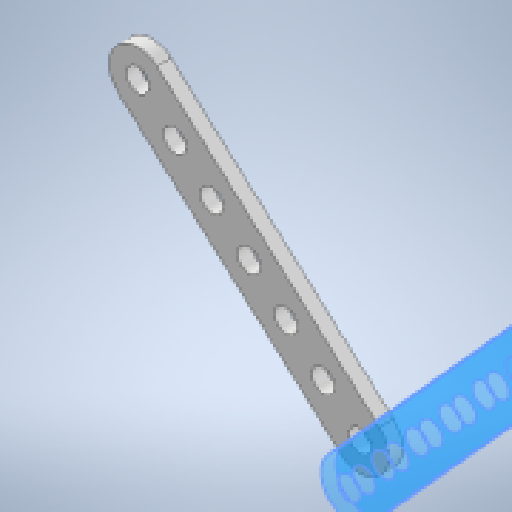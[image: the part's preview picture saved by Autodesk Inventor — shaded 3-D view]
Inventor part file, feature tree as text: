
AUTODESK INVENTOR PART (.ipt)
format: ipt  version: 2024.1 (Build 281209000, 209)  size: 167,936 bytes
history: native  units: mm
features: other x3, extrude x1, fillet x1, sketch x1, reference x1
ambient origin geometry x8: Origin, YZ Plane, XZ Plane, XY Plane, X Axis, Y Axis, Z Axis, Center Point
bodies: Solid1 (feature_tree)
feature tree (7):
  extrude  "Extrusion1"  Depth=4.0mm
  fillet  "Fillet1"  Radius=4.0mm
  sketch  "Sketch1"  dims[d0=8.0mm d1=4.0mm d2=4.0mm d3=70.0mm d5=7.0mm d6=10.0mm d8=10.0mm d10=4.0mm d11=2.0mm d12=0.0mm d13=4.0mm]
  reference  "Reference1"
  other  "<userpath>\Documents\0004-CAD\3D-cad-main\the-artifact\artifact-assembly.iam"
  other  "artifact-assembly.iam"
  other  "anchor-point:1"
